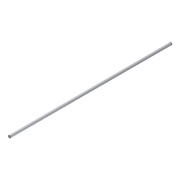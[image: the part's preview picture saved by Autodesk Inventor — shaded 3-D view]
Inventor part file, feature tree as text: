
AUTODESK INVENTOR PART (.ipt)
format: ipt  version: 2012 (Build 160160000, 160)  size: 62,976 bytes
history: native  units: in
note: dims shown in document units (in); Inventor stores cm internally (conversion verified against a paired STEP export)
features: extrude x1, plane x1, sketch x1, other x1
ambient origin geometry x8: Origin, YZ Plane, XZ Plane, XY Plane, X Axis, Y Axis, Z Axis, Center Point
bodies: Solid1 (feature_tree)
feature tree (4):
  extrude  "Extrusion1"  Depth=16.0in TaperAngle=0.0deg
  plane  "Work Plane1"
  sketch  "Sketch1"  dims[d0=0.25in d1=16.0in d2=0.0in d3=90.0deg]
  other  "Work Axis1"
